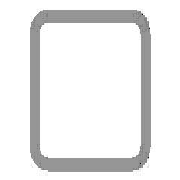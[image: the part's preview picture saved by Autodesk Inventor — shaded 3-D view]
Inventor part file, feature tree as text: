
AUTODESK INVENTOR PART (.ipt)
format: ipt  version: 2024 (Build 280153000, 153)  size: 128,512 bytes
history: native  units: mm (DEFAULTED — no unit token found)
features: other x4, extrude x1, sketch x1, plane x1
ambient origin geometry x8: Origin, YZ Plane, XZ Plane, XY Plane, X Axis, Y Axis, Z Axis, Center Point
bodies: Solid1 (feature_tree)
feature tree (7):
  parser-record x1  (decoder bookkeeping rows leaked as tree rows — omitted from the tree; the rows remain in map.json)
  other  "Driven Length"
  other  "Plano inicial"
  other  "Plano final"
  extrude  "Cuerpo"  TaperAngle=0.0deg  [1 undecoded]
  sketch  "Sketch3"  dims[d3=900.0mm d4=0.0mm d10=50.8mm d11=50.8mm d12=3.175mm d13=-0.0mm d14=900.0mm d15=25.4mm d16=25.4mm d17=6.35mm d18=90.0deg d19=900.0mm]
  plane  "Work Plane3"
note: 1 required parameter value undecoded (feature->parameter linkage not recoverable at this tier; creation-order binding heuristic only, values carry confidence <= 0.55)
